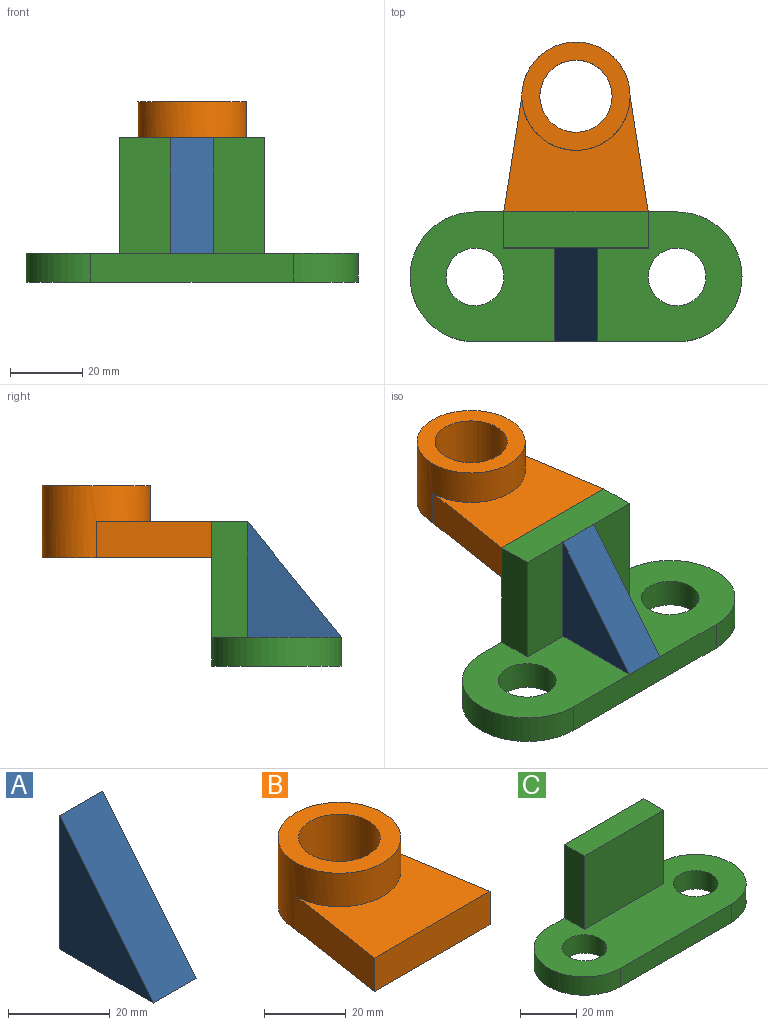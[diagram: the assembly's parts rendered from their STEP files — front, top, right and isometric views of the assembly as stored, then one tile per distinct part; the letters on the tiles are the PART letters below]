
ASSEMBLY  parts=3 mates=2
PART A: 5 faces, bbox 12x26x32 mm
  f0: plane 32x12mm, normal (0,1,0), area 384mm2, adj f1,f2,f3,f4
  f1: plane 26x12mm, normal (0,0,-1), area 312mm2, adj f0,f2,f3,f4
  f2: plane 32x26mm, normal (0,-0.78,0.63), area 494.8mm2, adj f0,f1,f3,f4
  f3: plane 32x26mm, normal (-1,0,0), area 416mm2, adj f0,f1,f2
  f4: plane 32x26mm, normal (1,0,0), area 416mm2, adj f0,f1,f2
PART B: 8 faces, bbox 40x47x20 mm
  f0: plane 40x32mm, normal (0,0,1), area 766.6mm2, adj f1,f2,f3,f4
  f1: plane 40x10mm, normal (0,-1,0), area 400mm2, adj f0,f2,f4,f6
  f2: plane 32x10mm, normal (0.99,0.15,0), area 323.9mm2, adj f0,f1,f3,f6
  f3: cylinder r=15mm len=30mm, axis (0,0,-1), area 1413.7mm2, adj f0,f2,f4,f6,f7
  f4: plane 32x10mm, normal (-0.99,0.15,0), area 323.9mm2, adj f0,f1,f3,f6
  f5: cylinder r=10mm len=20mm, axis (0,0,-1), area 1256.6mm2, adj f6,f7
  f6: plane 47x40mm, normal (0,0,-1), area 1159.3mm2, adj f1,f2,f3,f4,f5
  f7: plane 30x30mm, normal (0,0,1), area 392.7mm2, adj f3,f5
PART C: 12 faces, bbox 92x36x40 mm
  f0: plane 92x36mm, normal (0,0,1), area 2231.8mm2, adj f1,f2,f3,f4,f5,f6,f8,f9
  f1: cylinder r=18mm len=36mm, axis (0,0,-1), area 452.4mm2, adj f0,f2,f4,f7
  f2: plane 56x40mm, normal (0,1,0), area 1728mm2, adj f0,f1,f3,f7,f9,f10,f11
  f3: cylinder r=18mm len=36mm, axis (0,0,-1), area 452.4mm2, adj f0,f2,f4,f7
  f4: plane 56x8mm, normal (0,-1,0), area 448mm2, adj f0,f1,f3,f7
  f5: cylinder r=8mm len=16mm, axis (0,0,-1), area 402.1mm2, adj f0,f7
  f6: cylinder r=8mm len=16mm, axis (0,0,-1), area 402.1mm2, adj f0,f7
  f7: plane 92x36mm, normal (0,0,-1), area 2631.8mm2, adj f1,f2,f3,f4,f5,f6
  f8: plane 40x32mm, normal (0,-1,0), area 1280mm2, adj f0,f9,f10,f11
  f9: plane 32x10mm, normal (1,0,0), area 320mm2, adj f0,f2,f8,f11
  f10: plane 32x10mm, normal (-1,0,0), area 320mm2, adj f0,f2,f8,f11
  f11: plane 40x10mm, normal (0,0,1), area 400mm2, adj f2,f8,f9,f10
PLACE A t=(-67.67,-55.78,19.41)mm
PLACE B t=(-55.67,-57.78,41.41)mm
PLACE C t=(-55.67,-59.78,11.41)mm
MATE fastened B.f1 <-> C.f2  axis (0,-1,0) through (-55.67,-57.78,46.41)mm
MATE fastened C.f8 <-> A.f0  axis (0,-1,0) through (-55.67,-67.78,35.41)mm
